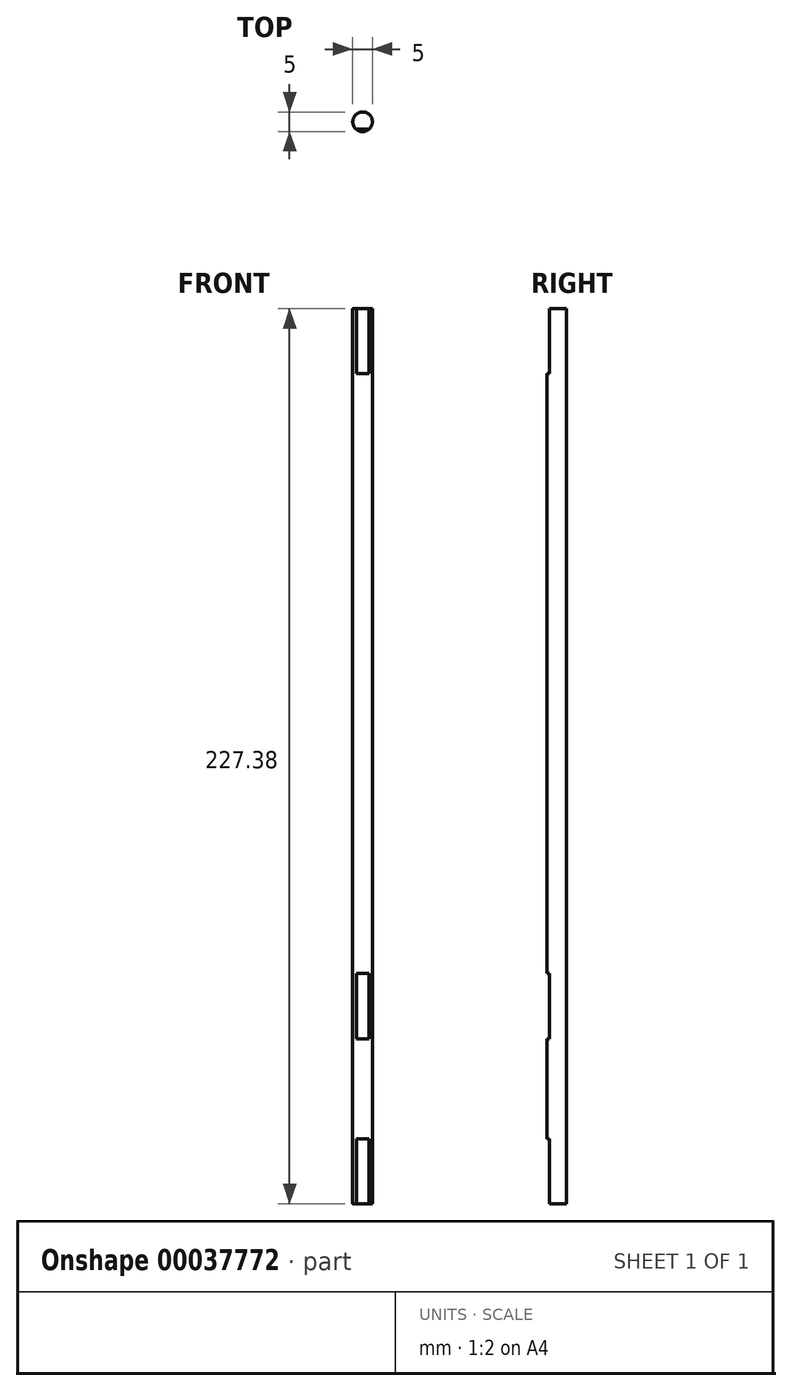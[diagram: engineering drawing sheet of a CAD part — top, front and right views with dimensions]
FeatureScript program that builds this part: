
annotation { "Feature Type Name" : "Feature", "Feature Type Description" : "" }
export const myFeature = defineFeature(function(context is Context, id is Id, definition is map)
    precondition{}
    {
        {
            var Q0;
            Q0=qCreatedBy(makeId("Top.planeOp"),FACE);
            var sketch = newSketch(context, id + "F0", { "sketchPlane" : qUnion([Q0])});
            skCircle(sketch, "E0", {"center": v(0, 0) * mm, "radius": 2.5 * mm});
            skSolve(sketch);
        }
        {
            var Q0;
            Q0 = qSketchRegion(id + "F0", true);
            extrude(context, id + "F1", {"entities" : qUnion([Q0]), "depth" : 152.4 * mm});
        }
        {
            var Q0;
            Q0=makeQuery(id+"F1.opExtrude","CAP_FACE",FACE,{"disambiguationData":[OSD([sQuery(id+"F0.wireOp",EDGE,"E0")])],"isStart":false});
            var sketch = newSketch(context, id + "F2", { "sketchPlane" : qUnion([Q0])});
            skArc(sketch, "E1", {"start": v(1.59, -1.93) * mm, "mid": v(0, 2.5) * mm, "end": v(-1.59, -1.93) * mm});
            skLineSegment(sketch, "E2", {"start": v(-1.59, -1.93) * mm, "end": v(1.59, -1.93) * mm});
            skLineSegment(sketch, "E3", {"start": v(0, 0) * mm, "end": v(0, -1.93) * mm});
            skSolve(sketch);
        }
        {
            var Q0;
            Q0 = qSketchRegion(id + "F2", true);
            extrude(context, id + "F3", {"entities" : qUnion([Q0]), "operationType" : NewBodyOperationType.ADD, "depth" : 16.53 * mm});
        }
        {
            var Q0;
            Q0=makeQuery(id+"F1.opExtrude","CAP_FACE",FACE,{"disambiguationData":[OSD([sQuery(id+"F0.wireOp",EDGE,"E0")])],"isStart":true});
            var sketch = newSketch(context, id + "F4", { "sketchPlane" : qUnion([Q0])});
            skArc(sketch, "E4", {"start": v(-1.59, 1.93) * mm, "mid": v(0, -2.5) * mm, "end": v(1.59, 1.93) * mm});
            skLineSegment(sketch, "E5", {"start": v(1.59, 1.93) * mm, "end": v(-1.59, 1.93) * mm});
            skSolve(sketch);
        }
        {
            var Q0;
            Q0 = qSketchRegion(id + "F4", true);
            extrude(context, id + "F5", {"entities" : qUnion([Q0]), "operationType" : NewBodyOperationType.ADD, "depth" : 16.53 * mm});
        }
        {
            var Q0;
            Q0=makeQuery(id+"F5.opExtrude","CAP_FACE",FACE,{"disambiguationData":[OSD([sQuery(id+"F4.wireOp",EDGE,"E4"),sQuery(id+"F4.wireOp",EDGE,"E5")])],"isStart":false});
            var sketch = newSketch(context, id + "F6", { "sketchPlane" : qUnion([Q0])});
            skCircle(sketch, "E6", {"center": v(0, 0) * mm, "radius": 2.5 * mm});
            skSolve(sketch);
        }
        {
            var Q0;
            Q0 = qSketchRegion(id + "F6", true);
            extrude(context, id + "F7", {"entities" : qUnion([Q0]), "operationType" : NewBodyOperationType.ADD, "depth" : 25.4 * mm});
        }
        {
            var Q0;
            Q0=makeQuery(id+"F7.opExtrude","CAP_FACE",FACE,{"disambiguationData":[OSD([sQuery(id+"F6.wireOp",EDGE,"E6")])],"isStart":false});
            var sketch = newSketch(context, id + "F8", { "sketchPlane" : qUnion([Q0])});
            skArc(sketch, "E7", {"start": v(-1.59, 1.93) * mm, "mid": v(0, -2.5) * mm, "end": v(1.59, 1.93) * mm});
            skLineSegment(sketch, "E8", {"start": v(-1.59, 1.93) * mm, "end": v(1.59, 1.93) * mm});
            skSolve(sketch);
        }
        {
            var Q0;
            Q0 = qSketchRegion(id + "F8", true);
            extrude(context, id + "F9", {"entities" : qUnion([Q0]), "operationType" : NewBodyOperationType.ADD, "depth" : 16.53 * mm});
        }
    });
